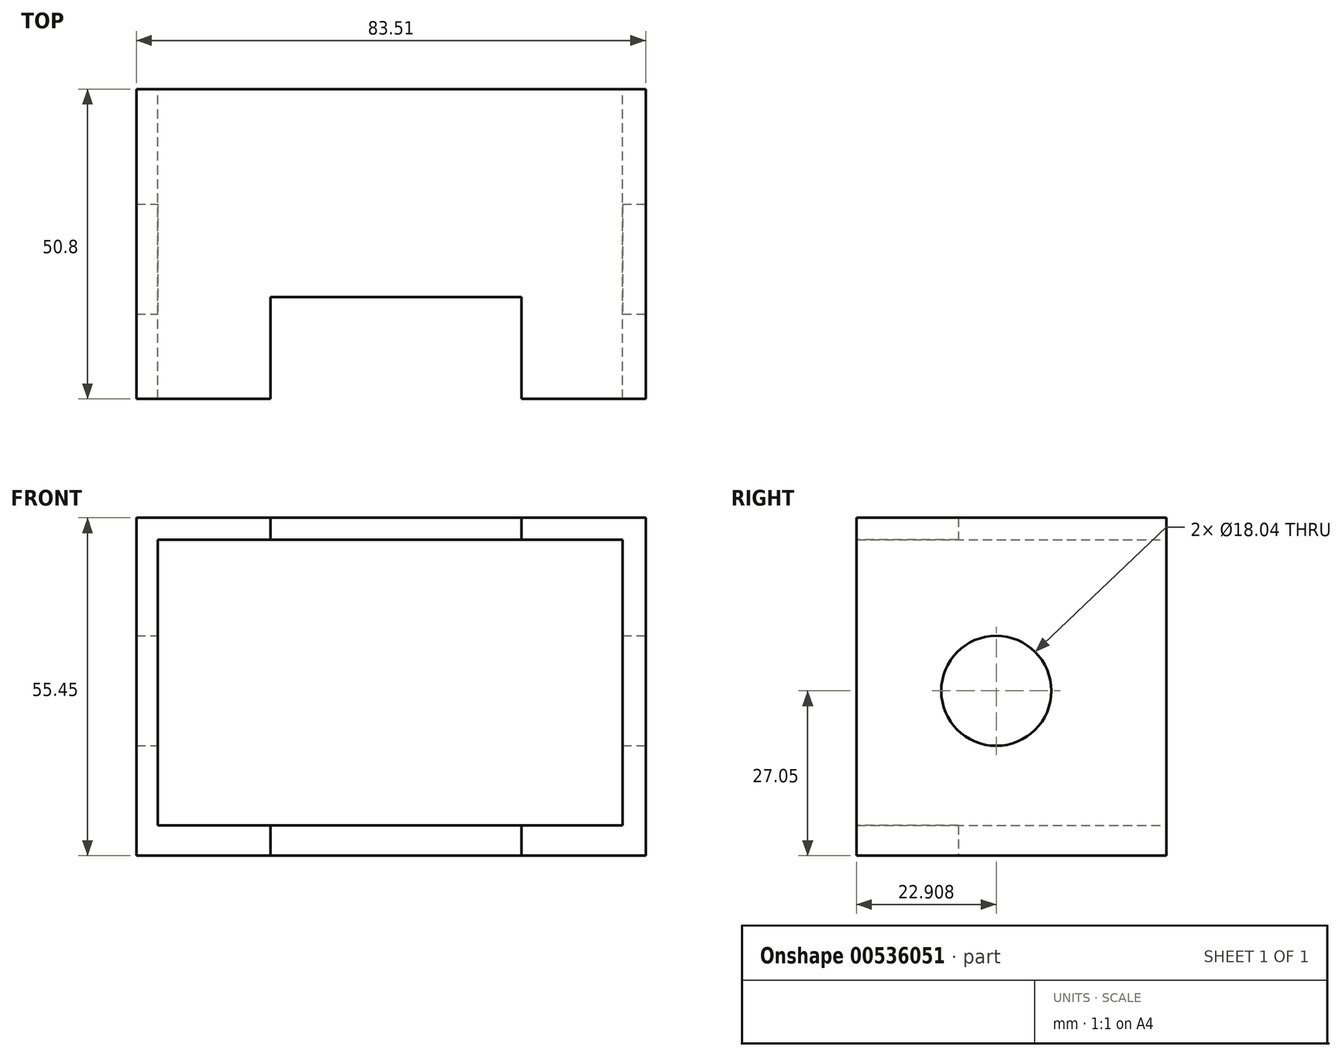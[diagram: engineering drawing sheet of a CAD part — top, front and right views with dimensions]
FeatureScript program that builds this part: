
annotation { "Feature Type Name" : "Feature", "Feature Type Description" : "" }
export const myFeature = defineFeature(function(context is Context, id is Id, definition is map)
    precondition{}
    {
        {
            var Q0;
            Q0=qCreatedBy(makeId("Front.planeOp"),FACE);
            var sketch = newSketch(context, id + "F0", { "sketchPlane" : qUnion([Q0])});
            skLineSegment(sketch, "E0.bottom", {"start": v(-40.32, 28.4) * mm, "end": v(43.2, 28.4) * mm});
            skLineSegment(sketch, "E0.top", {"start": v(-40.32, -27.05) * mm, "end": v(43.2, -27.05) * mm});
            skLineSegment(sketch, "E0.left", {"start": v(-40.32, 28.4) * mm, "end": v(-40.32, -27.05) * mm});
            skLineSegment(sketch, "E0.right", {"start": v(43.2, 28.4) * mm, "end": v(43.2, -27.05) * mm});
            skLineSegment(sketch, "E1.bottom", {"start": v(-36.82, 24.8) * mm, "end": v(39.37, 24.8) * mm});
            skLineSegment(sketch, "E1.top", {"start": v(-36.82, -22.09) * mm, "end": v(39.37, -22.09) * mm});
            skLineSegment(sketch, "E1.left", {"start": v(-36.82, 24.8) * mm, "end": v(-36.82, -22.09) * mm});
            skLineSegment(sketch, "E1.right", {"start": v(39.37, 24.8) * mm, "end": v(39.37, -22.09) * mm});
            skSolve(sketch);
        }
        {
            var Q0;
            Q0=makeQuery(id+"F0.imprint","IMPRINT",FACE,{"disambiguationData":[TD([[makeQuery(id+"F0.imprint","IMPRINT",EDGE,{"derivedFrom":sQuery(id+"F0.wireOp",EDGE,"E0.bottom")}),-1.0]])]});
            extrude(context, id + "F1", {"entities" : qUnion([Q0]), "depth" : 50.8 * mm, "offsetDistance" : 25.4 * mm});
        }
        {
            var Q0;
            Q0=makeQuery(id+"F1.opExtrude","SWEPT_FACE",FACE,{"disambiguationData":[OSD([sQuery(id+"F0.wireOp",EDGE,"E0.right")])]});
            var sketch = newSketch(context, id + "F2", { "sketchPlane" : qUnion([Q0])});
            skCircle(sketch, "E2", {"center": v(-27.9, 0) * mm, "radius": 9.02 * mm});
            skSolve(sketch);
        }
        {
            var Q0;
            Q0=makeQuery(id+"F2.imprint","IMPRINT",FACE,{"disambiguationData":[TD([[makeQuery(id+"F2.imprint","IMPRINT",EDGE,{"derivedFrom":sQuery(id+"F2.wireOp",EDGE,"E2")}),1.0]])]});
            extrude(context, id + "F3", {"entities" : qUnion([Q0]), "operationType" : NewBodyOperationType.REMOVE, "oppositeDirection" : true, "depth" : 113.28 * mm, "offsetDistance" : 25.4 * mm});
        }
        {
            var Q0;
            Q0=makeQuery(id+"F1.opExtrude","SWEPT_FACE",FACE,{"disambiguationData":[OSD([sQuery(id+"F0.wireOp",EDGE,"E0.top")])]});
            var sketch = newSketch(context, id + "F4", { "sketchPlane" : qUnion([Q0])});
            skLineSegment(sketch, "E3.bottom", {"start": v(-18.33, 50.8) * mm, "end": v(22.8, 50.8) * mm});
            skLineSegment(sketch, "E3.top", {"start": v(-18.33, 34.1) * mm, "end": v(22.8, 34.1) * mm});
            skLineSegment(sketch, "E3.left", {"start": v(-18.33, 50.8) * mm, "end": v(-18.33, 34.1) * mm});
            skLineSegment(sketch, "E3.right", {"start": v(22.8, 50.8) * mm, "end": v(22.8, 34.1) * mm});
            skSolve(sketch);
        }
        {
            var Q0;
            Q0=makeQuery(id+"F4.imprint","IMPRINT",FACE,{"disambiguationData":[TD([[makeQuery(id+"F4.imprint","IMPRINT",EDGE,{"derivedFrom":sQuery(id+"F4.wireOp",EDGE,"E3.bottom")}),-1.0]])]});
            extrude(context, id + "F5", {"entities" : qUnion([Q0]), "operationType" : NewBodyOperationType.REMOVE, "oppositeDirection" : true, "depth" : 1117.6 * mm, "offsetDistance" : 25.4 * mm});
        }
    });
